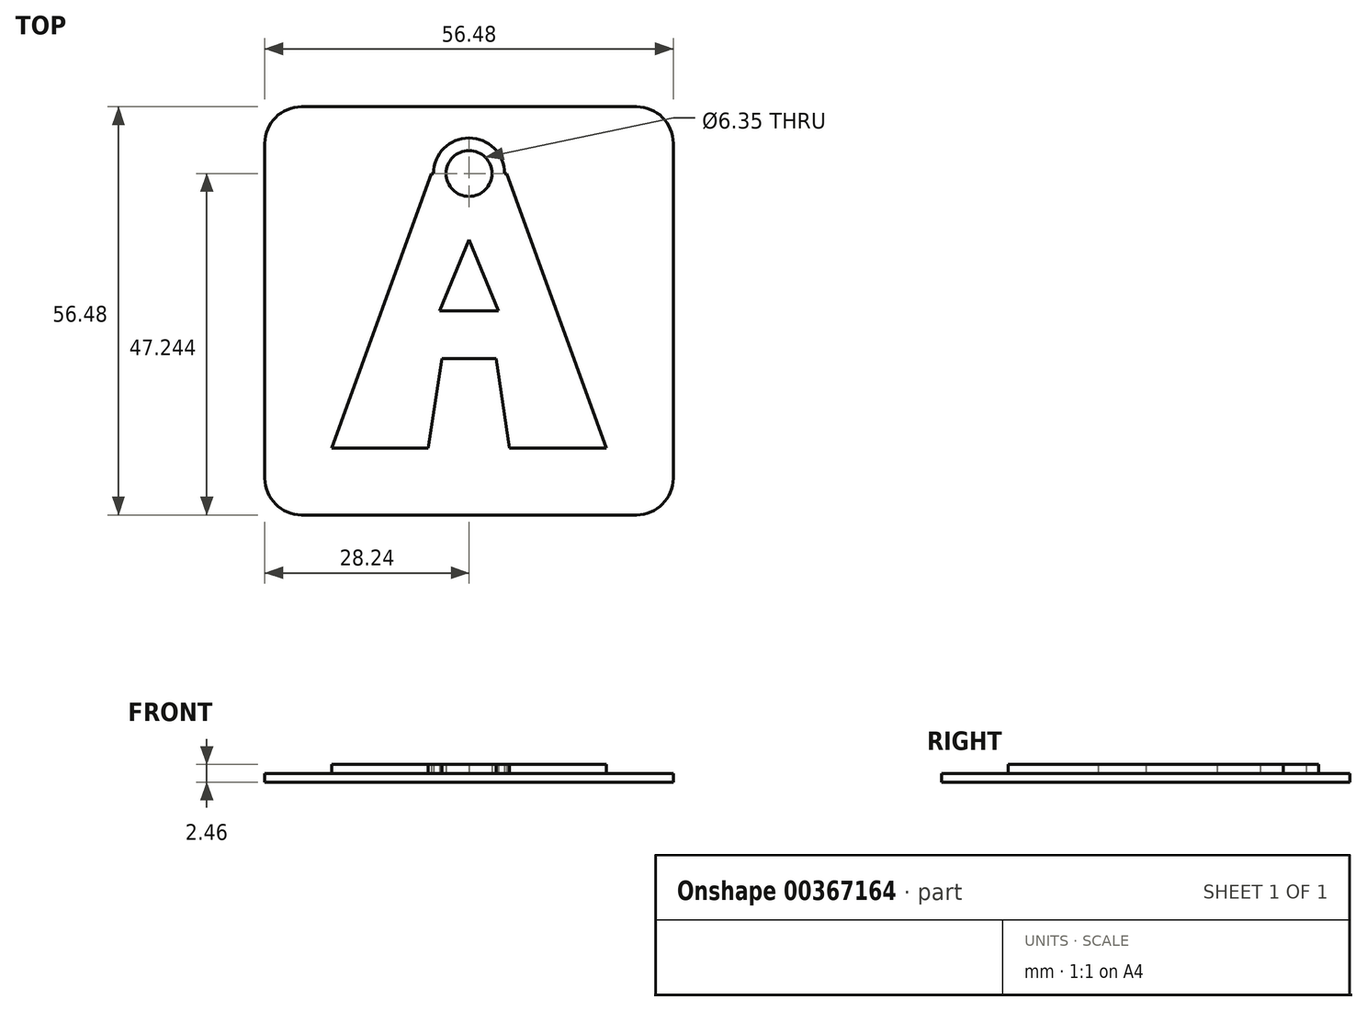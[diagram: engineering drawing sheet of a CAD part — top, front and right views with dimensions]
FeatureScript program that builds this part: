
annotation { "Feature Type Name" : "Feature", "Feature Type Description" : "" }
export const myFeature = defineFeature(function(context is Context, id is Id, definition is map)
    precondition{}
    {
        {
            var Q0;
            Q0=qCreatedBy(makeId("Top.planeOp"),FACE);
            var sketch = newSketch(context, id + "F0", { "sketchPlane" : qUnion([Q0])});
            skLineSegment(sketch, "E0.bottom", {"start": v(5.23, 19) * mm, "end": v(4.92, 19) * mm});
            skLineSegment(sketch, "E0.top", {"start": v(19, -19) * mm, "end": v(5.62, -19) * mm});
            skPoint(sketch, "E0.middle", {"position": v(0, 0) * mm});
            skLineSegment(sketch, "E1", {"start": v(-19, -19) * mm, "end": v(-5.23, 19) * mm});
            skLineSegment(sketch, "E2", {"start": v(-5.23, 19) * mm, "end": v(-4.92, 19) * mm});
            skLineSegment(sketch, "E3", {"start": v(5.23, 19) * mm, "end": v(19, -19) * mm});
            skLineSegment(sketch, "E4", {"start": v(-5.62, -19) * mm, "end": v(-3.74, -6.62) * mm});
            skLineSegment(sketch, "E5", {"start": v(-3.74, -6.62) * mm, "end": v(3.74, -6.62) * mm});
            skLineSegment(sketch, "E6", {"start": v(3.74, -6.62) * mm, "end": v(5.62, -19) * mm});
            skLineSegment(sketch, "E7", {"start": v(-4.05, 0) * mm, "end": v(4.05, 0) * mm});
            skLineSegment(sketch, "E8", {"start": v(4.05, 0) * mm, "end": v(0, 9.85) * mm});
            skLineSegment(sketch, "E9", {"start": v(0, 9.85) * mm, "end": v(-4.05, 0) * mm});
            skPoint(sketch, "E0.left.start.orphan", {"position": v(19, 19) * mm});
            skPoint(sketch, "E10.orphan", {"position": v(-19, 19) * mm});
            skLineSegment(sketch, "E11.trimOffspring", {"start": v(-5.62, -19) * mm, "end": v(-19, -19) * mm});
            skArc(sketch, "E12", {"start": v(4.92, 19) * mm, "mid": v(0, 23.92) * mm, "end": v(-4.92, 19) * mm});
            skLineSegment(sketch, "E13.trimOffspring", {"start": v(4.92, 19) * mm, "end": v(5.23, 19) * mm});
            skLineSegment(sketch, "E14.trimOffspring", {"start": v(-4.92, 19) * mm, "end": v(-5.23, 19) * mm});
            skCircle(sketch, "E15", {"center": v(0, 19) * mm, "radius": 3.18 * mm});
            skLineSegment(sketch, "E16.bottom", {"start": v(28.24, -28.24) * mm, "end": v(-28.24, -28.24) * mm});
            skLineSegment(sketch, "E16.top", {"start": v(28.24, 28.24) * mm, "end": v(-28.24, 28.24) * mm});
            skLineSegment(sketch, "E16.left", {"start": v(28.24, -28.24) * mm, "end": v(28.24, 28.24) * mm});
            skLineSegment(sketch, "E16.right", {"start": v(-28.24, -28.24) * mm, "end": v(-28.24, 28.24) * mm});
            skSolve(sketch);
        }
        {
            var Q0;
            Q0=makeQuery(id+"F0.imprint","IMPRINT",FACE,{"disambiguationData":[TD([[makeQuery(id+"F0.imprint","IMPRINT",EDGE,{"derivedFrom":sQuery(id+"F0.wireOp",EDGE,"E0.top")}),1.0]])]});
            var Q1;
            Q1=makeQuery(id+"F0.imprint","IMPRINT",FACE,{"disambiguationData":[TD([[makeQuery(id+"F0.imprint","IMPRINT",EDGE,{"derivedFrom":sQuery(id+"F0.wireOp",EDGE,"E7")}),1.0]])]});
            extrude(context, id + "F1", {"entities" : qUnion([Q0, Q1]), "depth" : 1.18 * mm});
        }
        {
            var Q0;
            Q0=makeQuery(id+"F0.imprint","IMPRINT",FACE,{"disambiguationData":[TD([[makeQuery(id+"F0.imprint","IMPRINT",EDGE,{"derivedFrom":sQuery(id+"F0.wireOp",EDGE,"E0.top")}),-1.0]])]});
            extrude(context, id + "F2", {"entities" : qUnion([Q0]), "operationType" : NewBodyOperationType.ADD, "depth" : 2.46 * mm});
        }
        {
            var Q0;
            Q0=makeQuery(id+"F1.opExtrude","SWEPT_EDGE",EDGE,{"disambiguationData":[OSD([sQuery(id+"F0.wireOp",EDGE,"E16.top"),sQuery(id+"F0.wireOp",EDGE,"E16.left")])]});
            var Q1;
            Q1=makeQuery(id+"F1.opExtrude","SWEPT_EDGE",EDGE,{"disambiguationData":[OSD([sQuery(id+"F0.wireOp",EDGE,"E16.top"),sQuery(id+"F0.wireOp",EDGE,"E16.right")])]});
            var Q2;
            Q2=makeQuery(id+"F1.opExtrude","SWEPT_EDGE",EDGE,{"disambiguationData":[OSD([sQuery(id+"F0.wireOp",EDGE,"E16.bottom"),sQuery(id+"F0.wireOp",EDGE,"E16.right")])]});
            var Q3;
            Q3=makeQuery(id+"F1.opExtrude","SWEPT_EDGE",EDGE,{"disambiguationData":[OSD([sQuery(id+"F0.wireOp",EDGE,"E16.bottom"),sQuery(id+"F0.wireOp",EDGE,"E16.left")])]});
            fillet(context, id + "F3", {"entities" : qUnion([Q0, Q1, Q2, Q3]), "radius" : 5.08 * mm, "tangentPropagation" : true, "allowEdgeOverflow" : false});
        }
    });
